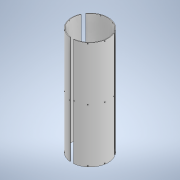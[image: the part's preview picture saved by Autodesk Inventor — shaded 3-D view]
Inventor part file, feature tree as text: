
AUTODESK INVENTOR PART (.ipt)
format: ipt  version: 2021 (Build 250183000, 183)  size: 354,816 bytes
history: native  units: in
note: dims shown in document units (in); Inventor stores cm internally (conversion verified against a paired STEP export)
features: other x34, hole x11, pattern_circular x8, sketch x8, plane x5, extrude x2
ambient origin geometry x8: Origin, YZ Plane, XZ Plane, XY Plane, X Axis, Y Axis, Z Axis, Center Point
bodies: Solid1 (feature_tree)
feature tree (68):
  extrude  "Extrusion1"  TaperAngle=0.0deg  [1 undecoded]
  plane  "Work Plane1"
  extrude  "Extrusion2"  Depth=0.3937in TaperAngle=0.0deg
  pattern_circular  "Circular Pattern1"  Count=3 Angle=360.0deg
  other  "Work Axis1"
  other  "Work Axis2"
  other  "Work Axis3"
  other  "Work Axis4"
  other  "Work Point1"
  other  "Work Point2"
  other  "Work Point3"
  other  "Central Plane"
  other  "Work Point4"
  other  "Work Axis6"
  other  "Work Axis7"
  other  "Offset Plane A"
  other  "Work Point5"
  other  "Work Point6"
  other  "Work Axis8"
  other  "Work Axis9"
  other  "Work Point7"
  other  "Work Point8"
  plane  "Work Plane5"
  plane  "Work Plane6"
  hole  "Hole1"  [1 undecoded]
  hole  "Hole2"  [1 undecoded]
  pattern_circular  "Circular Pattern3"  Count=3 Angle=360.0deg
  sketch  "Sketch5"  dims[d13=0.0484in d14=-11.811in]
  plane  "Work Plane7"
  sketch  "Sketch6"  dims[d15=0.0484in d16=0.1574in]
  hole  "Hole3"  [1 undecoded]
  other  "Work Axis10"
  hole  "Hole4"  [1 undecoded]
  pattern_circular  "Circular Pattern5"  Angle=60.0deg  [1 undecoded]
  plane  "Work Plane12"
  hole  "Hole5"  [1 undecoded]
  pattern_circular  "Circular Pattern6"  [2 undecoded]
  other  "plane for insert hole 1"
  sketch  "Sketch7"  dims[d17=-0.1574in]
  other  "plane for insert hole 2"
  sketch  "Sketch8"  dims[d48=1.0in d49=1.0in d29=0.096in d30=0.75in d31=0.185in d32=0.25in d33=0.5635in d34=1.0in d35=0.0in]
  hole  "insert hole 2"  [1 undecoded]
  hole  "insert hole 1"  [1 undecoded]
  pattern_circular  "Circular Pattern7"  [2 undecoded]
  pattern_circular  "Circular Pattern9"  [2 undecoded]
  other  "Work Axis14"
  other  "Work Axis16"
  other  "Work Point11"
  other  "Work Point12"
  other  "cap hardware plane 1"
  other  "cap hardware plane 2"
  sketch  "Sketch9"  dims[d52=1.0in d53=1.0in d38=0.096in d39=0.75in d40=0.185in d41=0.25in d42=0.5635in d43=1.0in d44=0.8108in d45=1.1811in d46=360.0deg]
  sketch  "Sketch10"  dims[d51=0.38in d54=0.177in d55=0.328in d56=0.332in d57=0.25in d58=0.5635in d59=0.484in d60=0.8108in d64=0.19in d65=0.177in d66=0.3229in d67=0.332in d68=0.25in d69=0.5635in d70=0.484in d71=0.8108in d72=1.5748in d73=360.0deg d75=60.0deg d76=1.0in d77=1.0in d78=0.129in d79=0.3229in d80=0.225in d81=0.25in d82=0.5635in d83=0.484in d84=0.8108in d85=1.1811in d86=360.0deg d88=0.2749in d89=0.2749in d90=0.0in d91=0.0in d92=0.0in d93=11.811in d94=0.0in d95=11.811in d96=0.129in d97=0.224in d98=0.225in d99=0.25in d100=0.5635in d101=0.349in d102=0.8108in d103=0.129in d104=0.224in d105=0.225in d106=0.25in d107=0.5635in d108=0.349in d109=0.8108in d110=1.1811in d111=360.0deg d116=1.1811in d117=360.0deg d119=0.0in d120=30.0deg d121=30.0deg d124=0.1969in d125=23.4252in d126=0.0in d127=0.0in d128=0.1969in d129=23.4252in d147=15.0deg d148=15.0deg d149=0.0in d150=0.0in d151=0.1969in d152=23.4252in d160=0.129in d161=0.75in d162=0.225in d163=0.25in d164=0.5635in d165=0.349in d166=0.8108in d167=0.129in d168=0.75in d169=0.225in d170=0.25in d171=0.5635in d172=0.349in d173=0.8108in d174=1.5748in d175=360.0deg d177=0.0in d178=0.0in d179=11.6142in d180=11.6142in d181=0.0in d182=0.0in d183=11.6142in d184=11.6142in d185=0.129in d186=0.75in d187=0.225in d188=0.25in d189=0.5635in d190=0.349in d191=0.8108in d192=0.129in d193=0.75in d194=0.225in d195=0.25in d196=0.5635in d197=0.349in d198=0.8108in d199=1.1811in d200=360.0deg d61=0.75in d62=0.8108in d63=0.0625in d130=1.0in d131=1.0in d132=1.0in d133=0.15in d134=0.25in d135=0.375in d136=0.5635in d137=0.75in d138=0.8108in d139=0.0625in d140=0.75in d141=0.375in]
  hole  "Quad Symmetry Holes 1"  [1 undecoded]
  hole  "Quad Symmetry Holes 2"  [1 undecoded]
  pattern_circular  "Circular Pattern11"  Count=30  [1 undecoded]
  hole  "Hole13"  [1 undecoded]
  hole  "Hole14"  [1 undecoded]
  pattern_circular  "Circular Pattern12"  [2 undecoded]
  sketch  "Sketch1"  dims[d3=0.0in d5=0.0in]
  sketch  "Sketch2"  dims[d7=0.3937in d8=0.5in d9=0.0in d10=1.1811in d11=360.0deg]
  other  "Work Axis5"
  other  "Offset Plane B"
  other  "Work Axis11"
  other  "Work Axis12"
  other  "Work Point9"
  other  "Work Axis13"
  other  "Work Point10"
note: 22 required parameter values undecoded (feature->parameter linkage not recoverable at this tier; creation-order binding heuristic only, values carry confidence <= 0.55)
